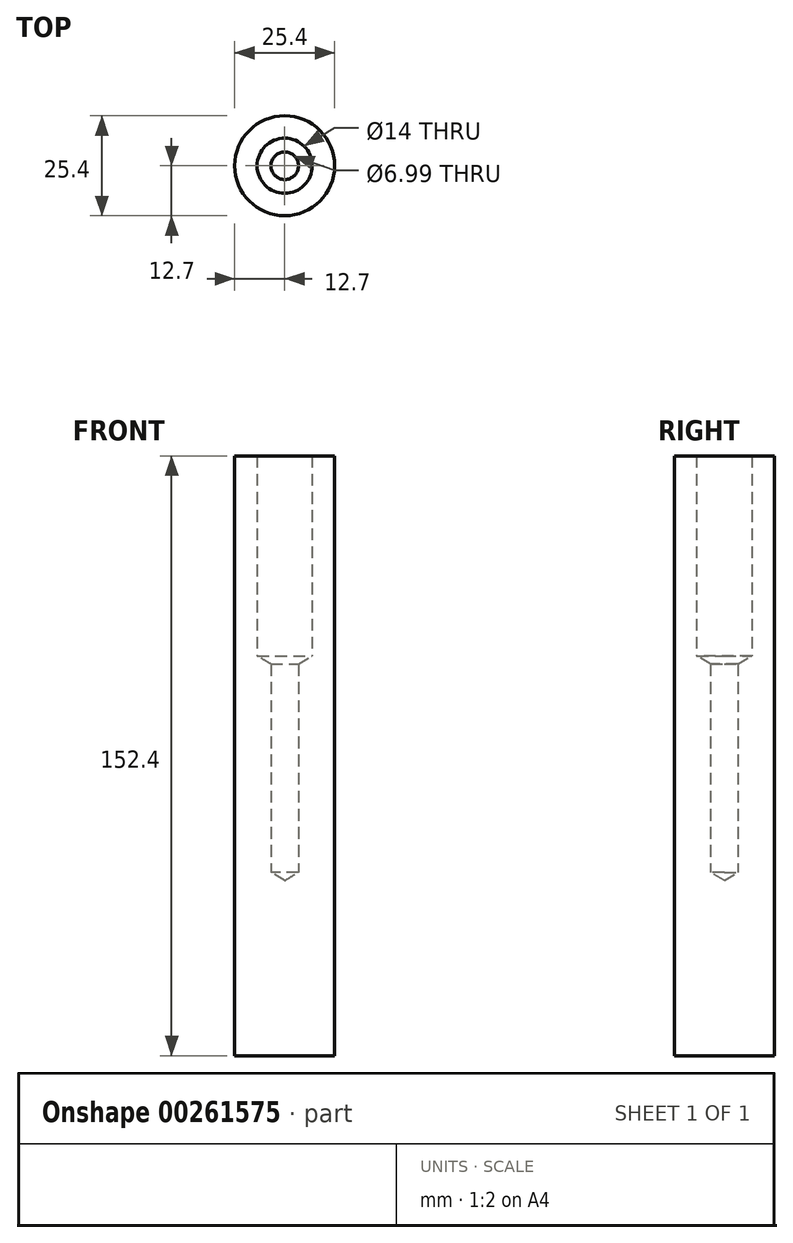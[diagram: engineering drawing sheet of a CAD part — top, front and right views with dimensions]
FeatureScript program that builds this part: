
annotation { "Feature Type Name" : "Feature", "Feature Type Description" : "" }
export const myFeature = defineFeature(function(context is Context, id is Id, definition is map)
    precondition{}
    {
        {
            var Q0;
            Q0=qCreatedBy(makeId("Top.planeOp"),FACE);
            var sketch = newSketch(context, id + "F0", { "sketchPlane" : qUnion([Q0])});
            skCircle(sketch, "E0", {"center": v(0, 0) * mm, "radius": 12.7 * mm});
            skSolve(sketch);
        }
        {
            var Q0;
            Q0=makeQuery(id+"F0.imprint","IMPRINT",FACE,{"disambiguationData":[TD([[makeQuery(id+"F0.imprint","IMPRINT",EDGE,{"derivedFrom":sQuery(id+"F0.wireOp",EDGE,"E0")}),1.0]])]});
            extrude(context, id + "F1", {"entities" : qUnion([Q0]), "depth" : 152.4 * mm});
        }
        {
            var Q0;
            Q0=makeQuery(id+"F1.opExtrude","CAP_FACE",FACE,{"disambiguationData":[OSD([sQuery(id+"F0.wireOp",EDGE,"E0")])],"isStart":false});
            var sketch = newSketch(context, id + "F2", { "sketchPlane" : qUnion([Q0])});
            skPoint(sketch, "E1", {"position": v(0, 0) * mm});
            skSolve(sketch);
        }
        {
            var Q0;
            Q0=sQuery(id+"F2.wireOp",VERTEX,"E1");
            var Q1;
            Q1=makeQuery(id+"F1.opExtrude","SWEPT_BODY",BODY,{"disambiguationData":[OSD([sQuery(id+"F0.wireOp",EDGE,"E0")])]});
            hole(context, id + "F3", {"style" : HoleStyle.SIMPLE, "endStyle" : HoleEndStyle.BLIND, "holeDiameter" : 14 * mm, "holeDepth" : 50.8 * mm, "tappedDepth" : 12.7 * mm, "tapClearance" : 3, "locations" : qUnion([Q0]), "scope" : qUnion([Q1])});
        }
        {
            var Q0;
            Q0=sQuery(id+"F2.wireOp",VERTEX,"E1");
            var Q1;
            Q1=makeQuery(id+"F1.opExtrude","SWEPT_BODY",BODY,{"disambiguationData":[OSD([sQuery(id+"F0.wireOp",EDGE,"E0")])]});
            hole(context, id + "F4", {"style" : HoleStyle.SIMPLE, "endStyle" : HoleEndStyle.BLIND, "holeDiameter" : 7 * mm, "holeDepth" : 50.8 * mm, "tappedDepth" : 12.7 * mm, "tapClearance" : 3, "locations" : qUnion([Q0]), "scope" : qUnion([Q1])});
        }
    });
